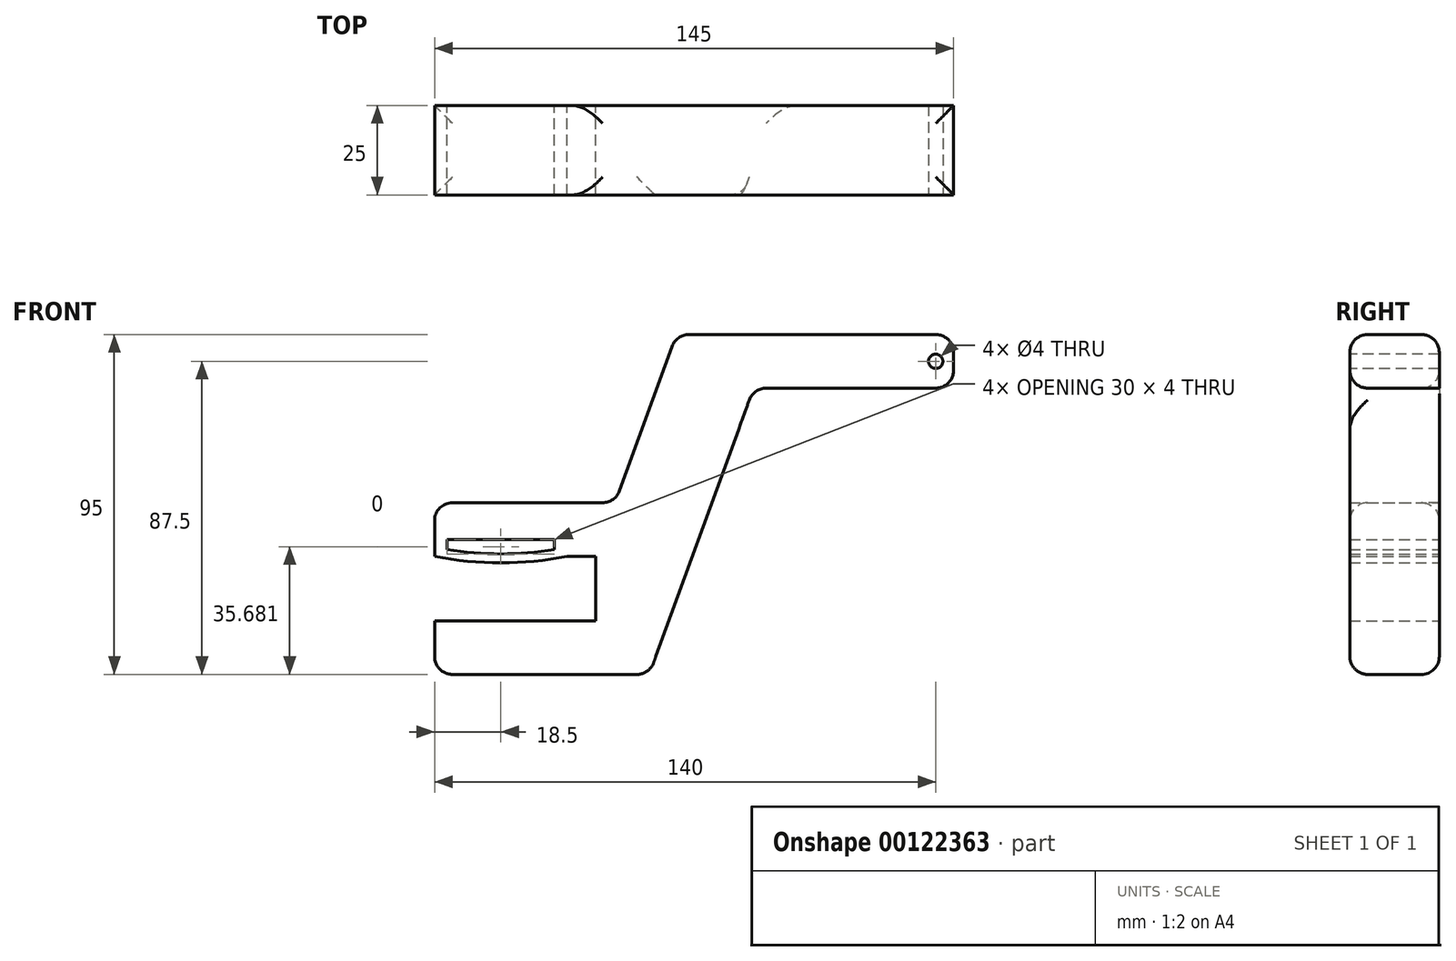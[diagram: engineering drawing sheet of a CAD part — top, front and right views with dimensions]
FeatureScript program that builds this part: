
annotation { "Feature Type Name" : "Feature", "Feature Type Description" : "" }
export const myFeature = defineFeature(function(context is Context, id is Id, definition is map)
    precondition{}
    {
        {
            var Q0;
            Q0=qCreatedBy(makeId("Front.planeOp"),FACE);
            var sketch = newSketch(context, id + "F0", { "sketchPlane" : qUnion([Q0])});
            skLineSegment(sketch, "E0", {"start": v(0, 15) * mm, "end": v(45, 15) * mm});
            skLineSegment(sketch, "E1", {"start": v(45, 15) * mm, "end": v(45, 33) * mm});
            skLineSegment(sketch, "E2", {"start": v(0, 33) * mm, "end": v(0, 48) * mm});
            skLineSegment(sketch, "E3", {"start": v(0, 48) * mm, "end": v(50.46, 48) * mm});
            skLineSegment(sketch, "E4", {"start": v(50.46, 48) * mm, "end": v(67.57, 95) * mm});
            skLineSegment(sketch, "E5", {"start": v(67.57, 95) * mm, "end": v(145, 95) * mm});
            skLineSegment(sketch, "E6", {"start": v(145, 95) * mm, "end": v(145, 80) * mm});
            skLineSegment(sketch, "E7", {"start": v(145, 80) * mm, "end": v(89.12, 80) * mm});
            skLineSegment(sketch, "E8", {"start": v(89.12, 80) * mm, "end": v(60, 0) * mm});
            skLineSegment(sketch, "E9", {"start": v(60, 0) * mm, "end": v(0, 0) * mm});
            skLineSegment(sketch, "E10", {"start": v(0, 0) * mm, "end": v(0, 15) * mm});
            skArc(sketch, "E11", {"start": v(0, 33) * mm, "mid": v(18.5, 31.18) * mm, "end": v(37, 33) * mm});
            skPoint(sketch, "E11.third.point", {"position": v(26.83, 220.82) * mm});
            skArc(sketch, "E12.0", {"start": v(3.5, 34.9) * mm, "mid": v(18.5, 33.68) * mm, "end": v(33.5, 34.9) * mm});
            skLineSegment(sketch, "E13", {"start": v(3.5, 37.68) * mm, "end": v(33.5, 37.68) * mm});
            skLineSegment(sketch, "E14", {"start": v(3.5, 37.68) * mm, "end": v(3.5, 34.9) * mm});
            skLineSegment(sketch, "E15", {"start": v(33.5, 37.68) * mm, "end": v(33.5, 34.9) * mm});
            skLineSegment(sketch, "E16", {"start": v(45, 33) * mm, "end": v(37, 33) * mm});
            skLineSegment(sketch, "E17", {"start": v(0, 0) * mm, "end": v(0, 66.32) * mm, "construction": true});
            skSolve(sketch);
        }
        {
            var Q0;
            Q0=makeQuery(id+"F0.imprint","IMPRINT",FACE,{"disambiguationData":[TD([[makeQuery(id+"F0.imprint","IMPRINT",EDGE,{"derivedFrom":sQuery(id+"F0.wireOp",EDGE,"E0")}),-1.0]])]});
            extrude(context, id + "F1", {"entities" : qUnion([Q0]), "depth" : 25 * mm});
        }
        {
            var Q0;
            Q0=makeQuery(id+"F1.opExtrude","SWEPT_EDGE",EDGE,{"disambiguationData":[OSD([sQuery(id+"F0.wireOp",EDGE,"E8"),sQuery(id+"F0.wireOp",EDGE,"E9")])]});
            var Q1;
            Q1=makeQuery(id+"F1.opExtrude","SWEPT_EDGE",EDGE,{"disambiguationData":[OSD([sQuery(id+"F0.wireOp",EDGE,"E7"),sQuery(id+"F0.wireOp",EDGE,"E8")])]});
            var Q2;
            Q2=makeQuery(id+"F1.opExtrude","SWEPT_EDGE",EDGE,{"disambiguationData":[OSD([sQuery(id+"F0.wireOp",EDGE,"E3"),sQuery(id+"F0.wireOp",EDGE,"E4")])]});
            var Q3;
            Q3=makeQuery(id+"F1.opExtrude","SWEPT_EDGE",EDGE,{"disambiguationData":[OSD([sQuery(id+"F0.wireOp",EDGE,"E4"),sQuery(id+"F0.wireOp",EDGE,"E5")])]});
            var Q4;
            Q4=makeQuery(id+"F1.opExtrude","SWEPT_EDGE",EDGE,{"disambiguationData":[OSD([sQuery(id+"F0.wireOp",EDGE,"E5"),sQuery(id+"F0.wireOp",EDGE,"E6")])]});
            var Q5;
            Q5=makeQuery(id+"F1.opExtrude","SWEPT_EDGE",EDGE,{"disambiguationData":[OSD([sQuery(id+"F0.wireOp",EDGE,"E6"),sQuery(id+"F0.wireOp",EDGE,"E7")])]});
            var Q6;
            Q6=makeQuery(id+"F1.opExtrude","SWEPT_EDGE",EDGE,{"disambiguationData":[OSD([sQuery(id+"F0.wireOp",EDGE,"E2"),sQuery(id+"F0.wireOp",EDGE,"E3")])]});
            var Q7;
            Q7=makeQuery(id+"F1.opExtrude","SWEPT_EDGE",EDGE,{"disambiguationData":[OSD([sQuery(id+"F0.wireOp",EDGE,"E9"),sQuery(id+"F0.wireOp",EDGE,"E10")])]});
            var Q8;
            Q8=makeQuery(id+"F1.opExtrude","CAP_EDGE",EDGE,{"disambiguationData":[OSD([sQuery(id+"F0.wireOp",EDGE,"E7")])],"isStart":false});
            var Q9;
            Q9=makeQuery(id+"F1.opExtrude","CAP_EDGE",EDGE,{"disambiguationData":[OSD([sQuery(id+"F0.wireOp",EDGE,"E8")])],"isStart":true});
            var Q10;
            Q10=makeQuery(id+"F1.opExtrude","CAP_EDGE",EDGE,{"disambiguationData":[OSD([sQuery(id+"F0.wireOp",EDGE,"E5")])],"isStart":false});
            var Q11;
            Q11=makeQuery(id+"F1.opExtrude","CAP_EDGE",EDGE,{"disambiguationData":[OSD([sQuery(id+"F0.wireOp",EDGE,"E4")])],"isStart":false});
            var Q12;
            Q12=makeQuery(id+"F1.opExtrude","CAP_EDGE",EDGE,{"disambiguationData":[OSD([sQuery(id+"F0.wireOp",EDGE,"E5")])],"isStart":true});
            var Q13;
            Q13=makeQuery(id+"F1.opExtrude","CAP_EDGE",EDGE,{"disambiguationData":[OSD([sQuery(id+"F0.wireOp",EDGE,"E4")])],"isStart":true});
            var Q14;
            Q14=makeQuery(id+"F1.opExtrude","CAP_EDGE",EDGE,{"disambiguationData":[OSD([sQuery(id+"F0.wireOp",EDGE,"E9")])],"isStart":false});
            var Q15;
            Q15=makeQuery(id+"F1.opExtrude","CAP_EDGE",EDGE,{"disambiguationData":[OSD([sQuery(id+"F0.wireOp",EDGE,"E9")])],"isStart":true});
            fillet(context, id + "F2", {"entities" : qUnion([Q0, Q1, Q2, Q3, Q4, Q5, Q6, Q7, Q8, Q9, Q10, Q11, Q12, Q13, Q14, Q15]), "radius" : 5 * mm, "tangentPropagation" : true, "allowEdgeOverflow" : false});
        }
        {
            var Q0;
            Q0=makeQuery(id+"F1.opExtrude","CAP_FACE",FACE,{"disambiguationData":[OSD([sQuery(id+"F0.wireOp",EDGE,"E0"),sQuery(id+"F0.wireOp",EDGE,"E1"),sQuery(id+"F0.wireOp",EDGE,"E2"),sQuery(id+"F0.wireOp",EDGE,"E3"),sQuery(id+"F0.wireOp",EDGE,"E4"),sQuery(id+"F0.wireOp",EDGE,"E5"),sQuery(id+"F0.wireOp",EDGE,"E6"),sQuery(id+"F0.wireOp",EDGE,"E7"),sQuery(id+"F0.wireOp",EDGE,"E8"),sQuery(id+"F0.wireOp",EDGE,"E9"),sQuery(id+"F0.wireOp",EDGE,"E10"),sQuery(id+"F0.wireOp",EDGE,"E11"),sQuery(id+"F0.wireOp",EDGE,"E12.0"),sQuery(id+"F0.wireOp",EDGE,"E13"),sQuery(id+"F0.wireOp",EDGE,"E14"),sQuery(id+"F0.wireOp",EDGE,"E15")])],"isStart":false});
            var sketch = newSketch(context, id + "F3", { "sketchPlane" : qUnion([Q0])});
            skCircle(sketch, "E18", {"center": v(140, 87.5) * mm, "radius": 2 * mm});
            skSolve(sketch);
        }
        {
            var Q0;
            Q0=makeQuery(id+"F3.imprint","IMPRINT",FACE,{"disambiguationData":[TD([[makeQuery(id+"F3.imprint","IMPRINT",EDGE,{"derivedFrom":sQuery(id+"F3.wireOp",EDGE,"E18")}),1.0]])]});
            extrude(context, id + "F4", {"entities" : qUnion([Q0]), "operationType" : NewBodyOperationType.REMOVE, "oppositeDirection" : true, "depth" : 25 * mm});
        }
    });
